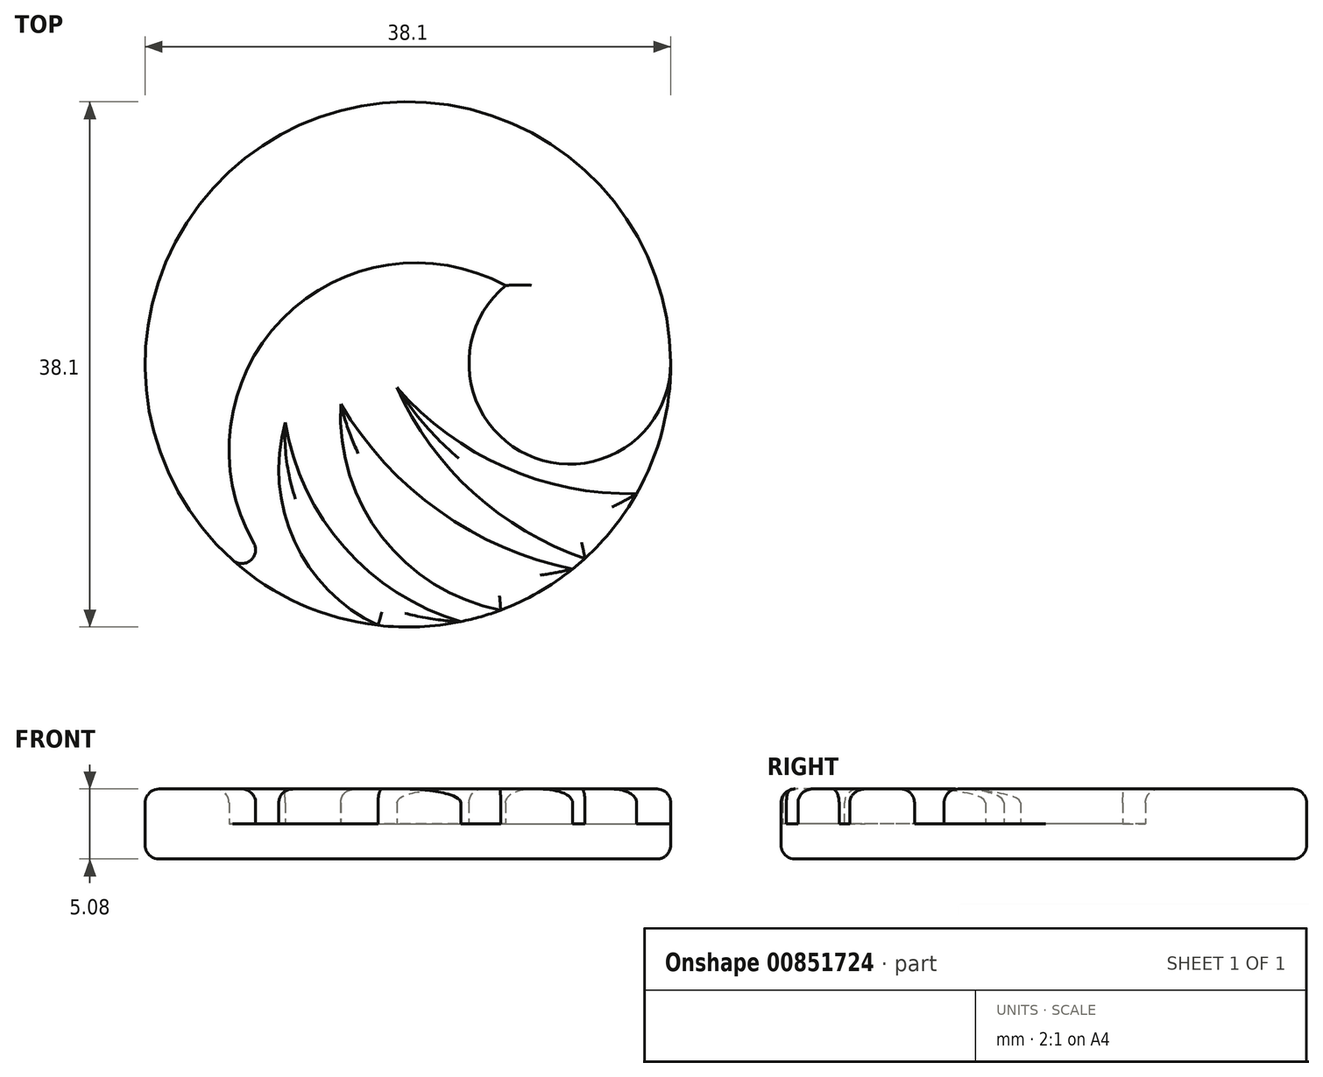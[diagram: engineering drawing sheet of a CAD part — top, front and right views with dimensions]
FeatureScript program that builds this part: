
annotation { "Feature Type Name" : "Feature", "Feature Type Description" : "" }
export const myFeature = defineFeature(function(context is Context, id is Id, definition is map)
    precondition{}
    {
        {
            var Q0;
            Q0=qCreatedBy(makeId("Top.planeOp"),FACE);
            var sketch = newSketch(context, id + "F0", { "sketchPlane" : qUnion([Q0])});
            skCircle(sketch, "E0", {"center": v(0, 0) * mm, "radius": 19.05 * mm});
            skSolve(sketch);
        }
        {
            var Q0;
            Q0 = qSketchRegion(id + "F0", true);
            extrude(context, id + "F1", {"entities" : qUnion([Q0]), "depth" : 2.54 * mm, "offsetDistance" : 25 * mm});
        }
        {
            var Q0;
            Q0=makeQuery(id+"F1.opExtrude","CAP_FACE",FACE,{"disambiguationData":[OSD([sQuery(id+"F0.wireOp",EDGE,"E0")])],"isStart":false});
            var sketch = newSketch(context, id + "F2", { "sketchPlane" : qUnion([Q0])});
            skCircle(sketch, "E1", {"center": v(11.74, 0.08) * mm, "radius": 7.31 * mm});
            skArc(sketch, "E2", {"start": v(7.08, 5.72) * mm, "mid": v(-11.32, 0.29) * mm, "end": v(-5.89, -18.12) * mm});
            skArc(sketch, "E3", {"start": v(-8.9, -4.22) * mm, "mid": v(-8.23, -12.81) * mm, "end": v(-2.17, -18.93) * mm});
            skArc(sketch, "E4", {"start": v(-8.9, -4.22) * mm, "mid": v(-4.61, -13.27) * mm, "end": v(3.83, -18.66) * mm});
            skArc(sketch, "E5", {"start": v(-4.86, -2.9) * mm, "mid": v(-1.87, -12.53) * mm, "end": v(6.73, -17.82) * mm});
            skArc(sketch, "E6", {"start": v(-4.86, -2.9) * mm, "mid": v(2.28, -10.64) * mm, "end": v(11.94, -14.84) * mm});
            skArc(sketch, "E7", {"start": v(-0.8, -1.67) * mm, "mid": v(4.72, -9.3) * mm, "end": v(12.84, -14.07) * mm});
            skArc(sketch, "E8", {"start": v(-0.8, -1.67) * mm, "mid": v(7.03, -7.47) * mm, "end": v(16.58, -9.38) * mm});
            skArc(sketch, "E9", {"start": v(-2.17, -18.93) * mm, "mid": v(0.84, -19.03) * mm, "end": v(3.83, -18.66) * mm});
            skArc(sketch, "E10", {"start": v(19.05, 0.13) * mm, "mid": v(-11.25, 15.38) * mm, "end": v(-5.89, -18.12) * mm});
            skArc(sketch, "E11", {"start": v(6.73, -17.82) * mm, "mid": v(9.45, -16.54) * mm, "end": v(11.94, -14.84) * mm});
            skArc(sketch, "E12", {"start": v(12.84, -14.07) * mm, "mid": v(14.9, -11.87) * mm, "end": v(16.58, -9.38) * mm});
            skLineSegment(sketch, "E13", {"start": v(-2.17, -18.93) * mm, "end": v(3.83, -18.66) * mm, "construction": true});
            skLineSegment(sketch, "E14", {"start": v(6.73, -17.82) * mm, "end": v(11.94, -14.84) * mm, "construction": true});
            skLineSegment(sketch, "E15", {"start": v(12.84, -14.07) * mm, "end": v(16.58, -9.38) * mm, "construction": true});
            skSolve(sketch);
        }
        {
            var Q0;
            Q0 = qSketchRegion(id + "F2", true);
            extrude(context, id + "F3", {"entities" : qUnion([Q0]), "operationType" : NewBodyOperationType.ADD, "depth" : 2.54 * mm, "offsetDistance" : 25 * mm});
        }
        {
            var Q0;
            Q0=makeQuery(id+"F3.opExtrude","CAP_FACE",FACE,{"disambiguationData":[OSD([sQuery(id+"F2.wireOp",EDGE,"E1"),sQuery(id+"F2.wireOp",EDGE,"E2"),sQuery(id+"F2.wireOp",EDGE,"E10")])],"isStart":false});
            var Q1;
            Q1=makeQuery(id+"F3.opExtrude","CAP_FACE",FACE,{"disambiguationData":[OSD([sQuery(id+"F2.wireOp",EDGE,"E5"),sQuery(id+"F2.wireOp",EDGE,"E6"),sQuery(id+"F2.wireOp",EDGE,"E11")])],"isStart":false});
            var Q2;
            Q2=makeQuery(id+"F3.opExtrude","CAP_FACE",FACE,{"disambiguationData":[OSD([sQuery(id+"F2.wireOp",EDGE,"E7"),sQuery(id+"F2.wireOp",EDGE,"E8"),sQuery(id+"F2.wireOp",EDGE,"E12")])],"isStart":false});
            var Q3;
            Q3=makeQuery(id+"F3.opExtrude","CAP_FACE",FACE,{"disambiguationData":[OSD([sQuery(id+"F2.wireOp",EDGE,"E3"),sQuery(id+"F2.wireOp",EDGE,"E4"),sQuery(id+"F2.wireOp",EDGE,"E9")])],"isStart":false});
            var Q4;
            Q4=makeQuery(id+"F3.opExtrude","SWEPT_EDGE",EDGE,{"disambiguationData":[OSD([sQuery(id+"F0.wireOp",EDGE,"E0"),sQuery(id+"F2.wireOp",EDGE,"E2"),sQuery(id+"F2.wireOp",EDGE,"E10")])]});
            var Q5;
            Q5=makeQuery(id+"F1.opExtrude","CAP_FACE",FACE,{"disambiguationData":[OSD([sQuery(id+"F0.wireOp",EDGE,"E0")])],"isStart":true});
            fillet(context, id + "F4", {"entities" : qUnion([Q0, Q1, Q2, Q3, Q4, Q5]), "radius" : 1 * mm, "allowEdgeOverflow" : false});
        }
    });
